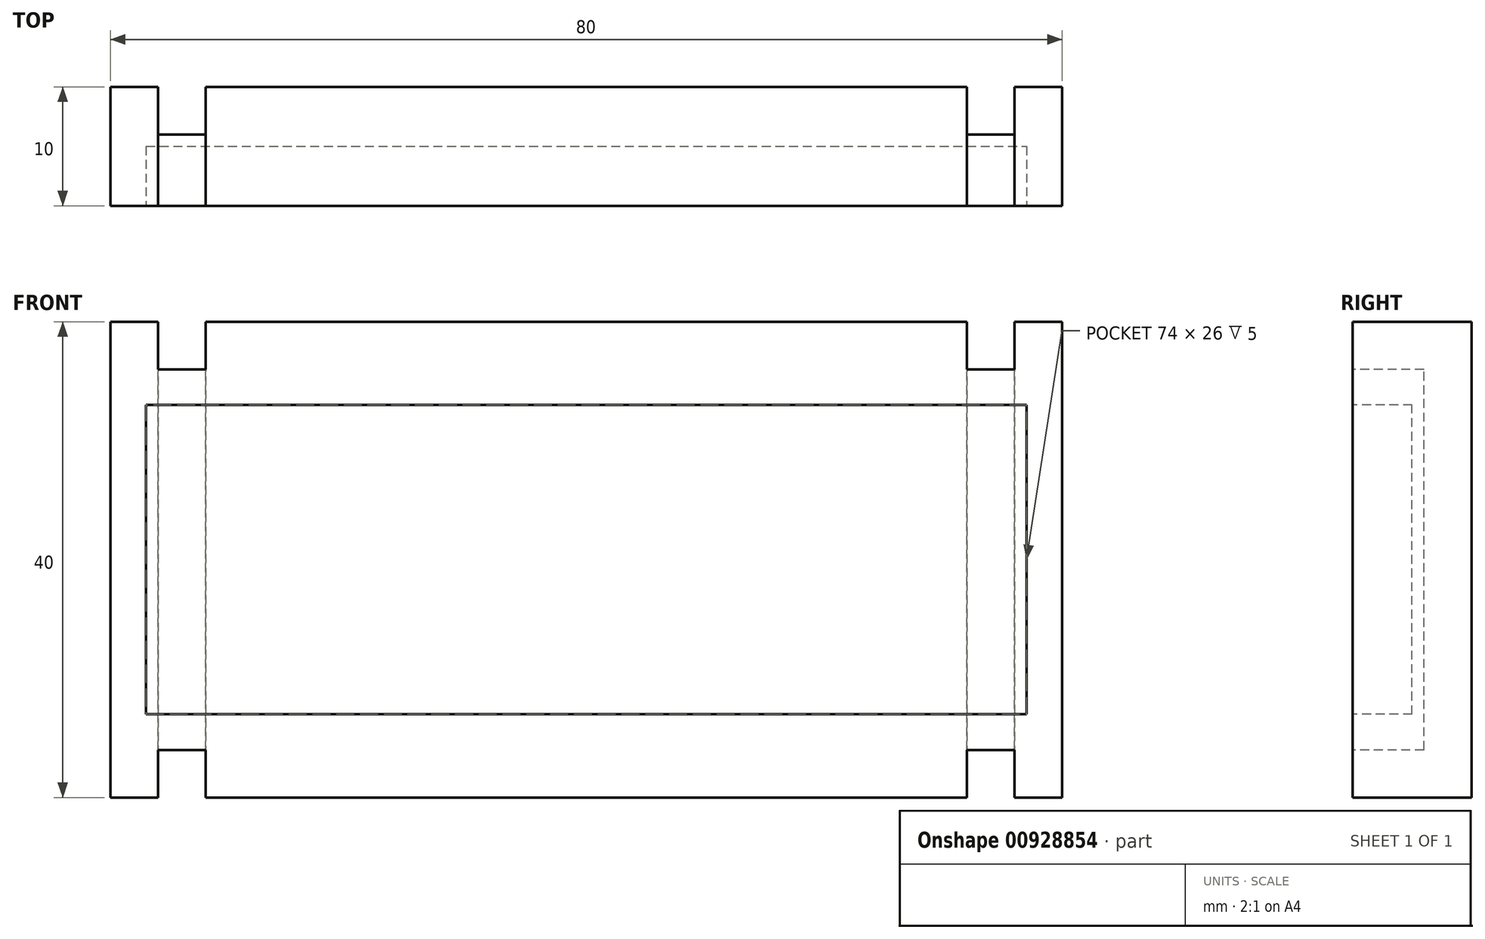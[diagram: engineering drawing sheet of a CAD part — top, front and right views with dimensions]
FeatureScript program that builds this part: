
annotation { "Feature Type Name" : "Feature", "Feature Type Description" : "" }
export const myFeature = defineFeature(function(context is Context, id is Id, definition is map)
    precondition{}
    {
        {
            var Q0;
            Q0=qCreatedBy(makeId("Front.planeOp"),FACE);
            var sketch = newSketch(context, id + "F0", { "sketchPlane" : qUnion([Q0])});
            skLineSegment(sketch, "E0.bottom", {"start": v(0, 0) * mm, "end": v(80, 0) * mm});
            skLineSegment(sketch, "E0.top", {"start": v(0, 40) * mm, "end": v(80, 40) * mm});
            skLineSegment(sketch, "E0.left", {"start": v(0, 0) * mm, "end": v(0, 40) * mm});
            skLineSegment(sketch, "E0.right", {"start": v(80, 0) * mm, "end": v(80, 40) * mm});
            skSolve(sketch);
        }
        {
            var Q0;
            Q0 = qSketchRegion(id + "F0", true);
            extrude(context, id + "F1", {"entities" : qUnion([Q0]), "depth" : 10 * mm, "offsetDistance" : 25.4 * mm});
        }
        {
            var Q0;
            Q0=makeQuery(id+"F1.opExtrude","CAP_FACE",FACE,{"disambiguationData":[OSD([sQuery(id+"F0.wireOp",EDGE,"E0.bottom"),sQuery(id+"F0.wireOp",EDGE,"E0.top"),sQuery(id+"F0.wireOp",EDGE,"E0.left"),sQuery(id+"F0.wireOp",EDGE,"E0.right")])],"isStart":false});
            var sketch = newSketch(context, id + "F2", { "sketchPlane" : qUnion([Q0])});
            skLineSegment(sketch, "E1.bottom", {"start": v(3, 7) * mm, "end": v(77, 7) * mm});
            skLineSegment(sketch, "E1.top", {"start": v(3, 33) * mm, "end": v(77, 33) * mm});
            skLineSegment(sketch, "E1.left", {"start": v(3, 7) * mm, "end": v(3, 33) * mm});
            skLineSegment(sketch, "E1.right", {"start": v(77, 7) * mm, "end": v(77, 33) * mm});
            skSolve(sketch);
        }
        {
            var Q0;
            Q0=makeQuery(id+"F2.imprint","IMPRINT",FACE,{"disambiguationData":[TD([[makeQuery(id+"F2.imprint","IMPRINT",EDGE,{"derivedFrom":sQuery(id+"F2.wireOp",EDGE,"E1.bottom")}),1.0]])]});
            extrude(context, id + "F3", {"entities" : qUnion([Q0]), "operationType" : NewBodyOperationType.REMOVE, "oppositeDirection" : true, "depth" : 5 * mm, "offsetDistance" : 25.4 * mm});
        }
        {
            var Q0;
            Q0=makeQuery(id+"F1.opExtrude","CAP_FACE",FACE,{"disambiguationData":[OSD([sQuery(id+"F0.wireOp",EDGE,"E0.bottom"),sQuery(id+"F0.wireOp",EDGE,"E0.top"),sQuery(id+"F0.wireOp",EDGE,"E0.left"),sQuery(id+"F0.wireOp",EDGE,"E0.right")])],"isStart":false});
            var sketch = newSketch(context, id + "F4", { "sketchPlane" : qUnion([Q0])});
            skLineSegment(sketch, "E2", {"start": v(40, 40) * mm, "end": v(40, 0) * mm, "construction": true});
            skLineSegment(sketch, "E3", {"start": v(0, 20) * mm, "end": v(80, 20) * mm, "construction": true});
            skLineSegment(sketch, "E4.bottom", {"start": v(4, 40) * mm, "end": v(8, 40) * mm});
            skLineSegment(sketch, "E4.top", {"start": v(4, 36) * mm, "end": v(8, 36) * mm});
            skLineSegment(sketch, "E4.left", {"start": v(4, 40) * mm, "end": v(4, 36) * mm});
            skLineSegment(sketch, "E4.right", {"start": v(8, 40) * mm, "end": v(8, 36) * mm});
            skLineSegment(sketch, "E5.MirrorCS", {"start": v(76, 40) * mm, "end": v(76, 36) * mm});
            skLineSegment(sketch, "E6.MirrorCS", {"start": v(72, 40) * mm, "end": v(72, 36) * mm});
            skLineSegment(sketch, "E7.MirrorCS", {"start": v(76, 36) * mm, "end": v(72, 36) * mm});
            skLineSegment(sketch, "E8.MirrorCS", {"start": v(76, 40) * mm, "end": v(72, 40) * mm});
            skLineSegment(sketch, "E9.MirrorCS", {"start": v(80, 20) * mm, "end": v(0, 20) * mm, "construction": true});
            skLineSegment(sketch, "E10.MirrorCS", {"start": v(76, 4) * mm, "end": v(72, 4) * mm});
            skLineSegment(sketch, "E11.MirrorCS", {"start": v(76, 0) * mm, "end": v(76, 4) * mm});
            skLineSegment(sketch, "E12.MirrorCS", {"start": v(76, 0) * mm, "end": v(72, 0) * mm});
            skLineSegment(sketch, "E13.MirrorCS", {"start": v(72, 0) * mm, "end": v(72, 4) * mm});
            skLineSegment(sketch, "E14.MirrorCS", {"start": v(4, 0) * mm, "end": v(8, 0) * mm});
            skLineSegment(sketch, "E15.MirrorCS", {"start": v(4, 0) * mm, "end": v(4, 4) * mm});
            skLineSegment(sketch, "E16.MirrorCS", {"start": v(8, 0) * mm, "end": v(8, 4) * mm});
            skLineSegment(sketch, "E17.MirrorCS", {"start": v(4, 4) * mm, "end": v(8, 4) * mm});
            skSolve(sketch);
        }
        {
            var Q0;
            Q0 = qSketchRegion(id + "F4", true);
            extrude(context, id + "F5", {"entities" : qUnion([Q0]), "operationType" : NewBodyOperationType.REMOVE, "oppositeDirection" : true, "depth" : 25.4 * mm, "offsetDistance" : 25.4 * mm});
        }
        {
            var Q0;
            {var subQ2=sQuery(id+"F0.wireOp",EDGE,"E0.top");Q0=makeQuery(id+"F5.boolean.opBoolean","SPLIT",FACE,{"disambiguationData":[TD([makeQuery(id+"F5.opExtrude","SWEPT_FACE",FACE,{"disambiguationData":[OSD([sQuery(id+"F4.wireOp",EDGE,"E4.right")])]})])],"derivedFrom":makeQuery(id+"F1.opExtrude","SWEPT_FACE",FACE,{"disambiguationData":[OSD([subQ2])]})});}
            var sketch = newSketch(context, id + "F6", { "sketchPlane" : qUnion([Q0])});
            skLineSegment(sketch, "E18.bottom", {"start": v(8, 0) * mm, "end": v(4, 0) * mm});
            skLineSegment(sketch, "E18.top", {"start": v(8, -4) * mm, "end": v(4, -4) * mm});
            skLineSegment(sketch, "E18.left", {"start": v(8, 0) * mm, "end": v(8, -4) * mm});
            skLineSegment(sketch, "E18.right", {"start": v(4, 0) * mm, "end": v(4, -4) * mm});
            skLineSegment(sketch, "E19", {"start": v(40, 0) * mm, "end": v(40, -10) * mm, "construction": true});
            skLineSegment(sketch, "E20.MirrorCS", {"start": v(72, -4) * mm, "end": v(76, -4) * mm});
            skLineSegment(sketch, "E21.MirrorCS", {"start": v(76, 0) * mm, "end": v(76, -4) * mm});
            skLineSegment(sketch, "E22.MirrorCS", {"start": v(72, 0) * mm, "end": v(72, -4) * mm});
            skLineSegment(sketch, "E23.MirrorCS", {"start": v(72, 0) * mm, "end": v(76, 0) * mm});
            skSolve(sketch);
        }
        {
            var Q0;
            Q0 = qSketchRegion(id + "F6", true);
            extrude(context, id + "F7", {"entities" : qUnion([Q0]), "operationType" : NewBodyOperationType.REMOVE, "oppositeDirection" : true, "depth" : 50.8 * mm, "offsetDistance" : 25.4 * mm});
        }
    });
